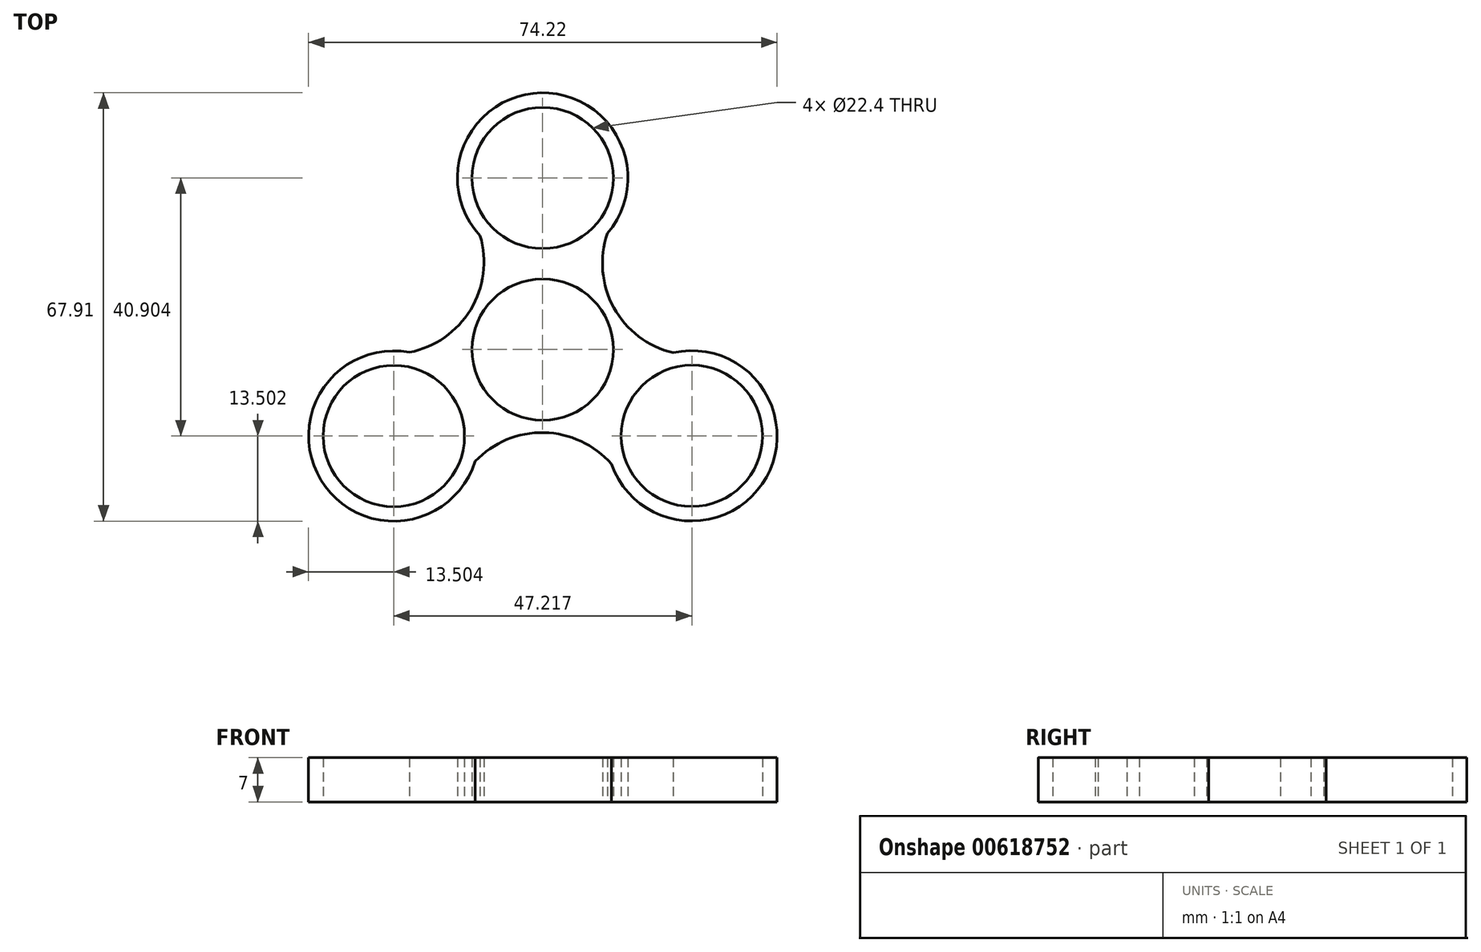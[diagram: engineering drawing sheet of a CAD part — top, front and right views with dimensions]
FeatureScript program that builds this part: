
annotation { "Feature Type Name" : "Feature", "Feature Type Description" : "" }
export const myFeature = defineFeature(function(context is Context, id is Id, definition is map)
    precondition{}
    {
        {
            var Q0;
            Q0=qCreatedBy(makeId("Top.planeOp"),FACE);
            var sketch = newSketch(context, id + "F0", { "sketchPlane" : qUnion([Q0])});
            skCircle(sketch, "E0", {"center": v(0, 0) * mm, "radius": 11.2 * mm});
            skCircle(sketch, "E1", {"center": v(0, 27.2) * mm, "radius": 11.2 * mm});
            skArc(sketch, "E2", {"start": v(10.25, 18.42) * mm, "mid": v(-0.25, 40.7) * mm, "end": v(-9.91, 18.04) * mm});
            skArc(sketch, "E3.1.0", {"start": v(-21.1, -0.43) * mm, "mid": v(-35.15, -20.67) * mm, "end": v(-10.7, -17.7) * mm});
            skCircle(sketch, "E3.1.1", {"center": v(-23.59, -13.7) * mm, "radius": 11.2 * mm});
            skArc(sketch, "E3.2.0", {"start": v(10.9, -18.16) * mm, "mid": v(35.45, -20.2) * mm, "end": v(20.65, -0.5) * mm});
            skCircle(sketch, "E3.2.1", {"center": v(23.63, -13.67) * mm, "radius": 11.2 * mm});
            skPoint(sketch, "E3.center", {"position": v(0.01, -0.05) * mm});
            skArc(sketch, "E4", {"start": v(-21.1, -0.43) * mm, "mid": v(-11.43, 6.33) * mm, "end": v(-9.91, 18.04) * mm});
            skArc(sketch, "E5.1.0", {"start": v(10.9, -18.16) * mm, "mid": v(0.2, -13.16) * mm, "end": v(-10.7, -17.7) * mm});
            skArc(sketch, "E5.2.0", {"start": v(10.25, 18.42) * mm, "mid": v(11.27, 6.66) * mm, "end": v(20.65, -0.5) * mm});
            skPoint(sketch, "E6.orphan", {"position": v(27.03, -0.6) * mm});
            skPoint(sketch, "E7.orphan", {"position": v(-13.97, -23.17) * mm});
            skPoint(sketch, "E8.orphan", {"position": v(-13.01, 23.62) * mm});
            skSolve(sketch);
        }
        {
            var Q0;
            Q0=makeQuery(id+"F0.imprint","IMPRINT",FACE,{"disambiguationData":[TD([[makeQuery(id+"F0.imprint","IMPRINT",EDGE,{"derivedFrom":sQuery(id+"F0.wireOp",EDGE,"E0")}),-1.0]])]});
            extrude(context, id + "F1", {"entities" : qUnion([Q0]), "depth" : 7 * mm, "offsetDistance" : 25 * mm});
        }
    });
